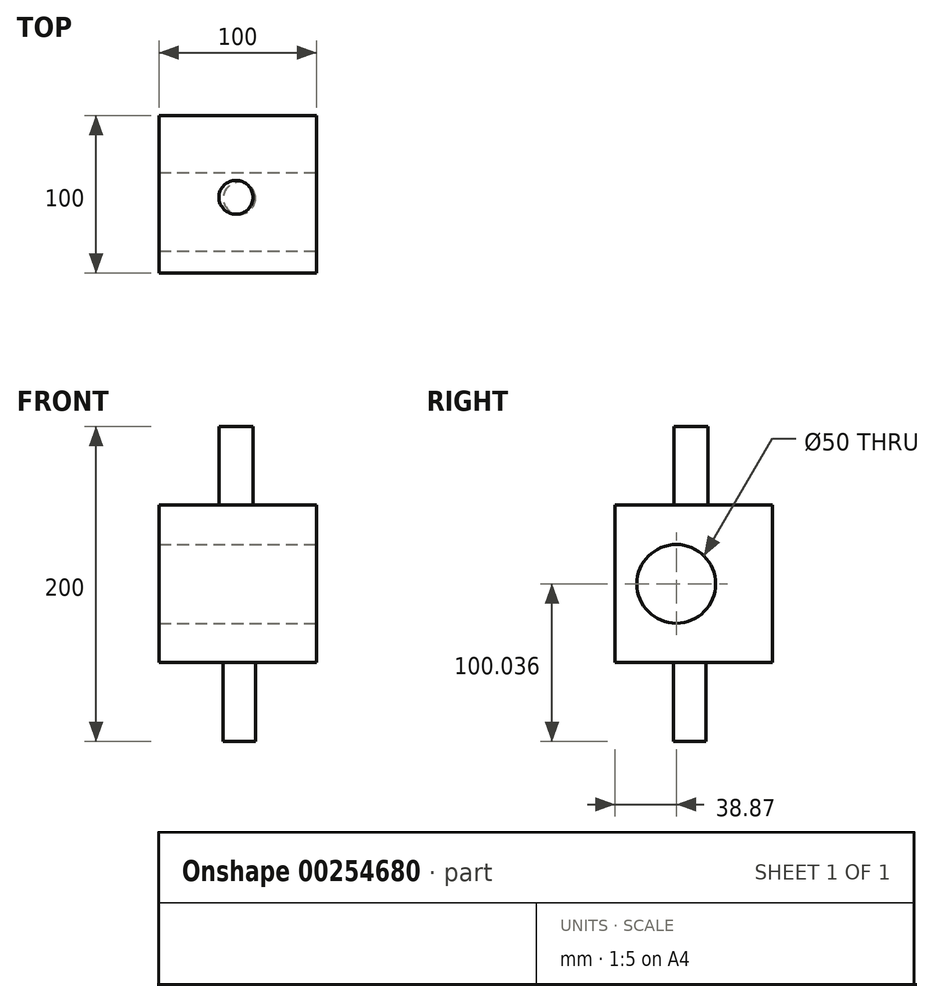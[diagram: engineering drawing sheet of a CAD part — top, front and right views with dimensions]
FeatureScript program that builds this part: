
annotation { "Feature Type Name" : "Feature", "Feature Type Description" : "" }
export const myFeature = defineFeature(function(context is Context, id is Id, definition is map)
    precondition{}
    {
        {
            var Q0;
            Q0=qCreatedBy(makeId("Front.planeOp"),FACE);
            var sketch = newSketch(context, id + "F0", { "sketchPlane" : qUnion([Q0])});
            skLineSegment(sketch, "E0.bottom", {"start": v(0, 0) * mm, "end": v(100, 0) * mm});
            skLineSegment(sketch, "E0.top", {"start": v(0, 100) * mm, "end": v(100, 100) * mm});
            skLineSegment(sketch, "E0.left", {"start": v(0, 0) * mm, "end": v(0, 100) * mm});
            skLineSegment(sketch, "E0.right", {"start": v(100, 0) * mm, "end": v(100, 100) * mm});
            skSolve(sketch);
        }
        {
            var Q0;
            Q0 = qSketchRegion(id + "F0", true);
            extrude(context, id + "F1", {"entities" : qUnion([Q0]), "depth" : 100 * mm});
        }
        {
            var Q0;
            Q0=makeQuery(id+"F1.opExtrude","SWEPT_FACE",FACE,{"disambiguationData":[OSD([sQuery(id+"F0.wireOp",EDGE,"E0.top")])]});
            var sketch = newSketch(context, id + "F2", { "sketchPlane" : qUnion([Q0])});
            skCircle(sketch, "E1", {"center": v(48.79, -51.93) * mm, "radius": 10.8 * mm});
            skSolve(sketch);
        }
        {
            var Q0;
            Q0 = qSketchRegion(id + "F2", true);
            extrude(context, id + "F3", {"entities" : qUnion([Q0]), "operationType" : NewBodyOperationType.ADD, "depth" : 50 * mm});
        }
        {
            var Q0;
            Q0=makeQuery(id+"F3.opExtrude","CAP_FACE",FACE,{"disambiguationData":[OSD([sQuery(id+"F2.wireOp",EDGE,"E1")])],"isStart":false});
            var sketch = newSketch(context, id + "F4", { "sketchPlane" : qUnion([Q0])});
            skSolve(sketch);
        }
        {
            var Q0;
            Q0=makeQuery(id+"F1.opExtrude","SWEPT_FACE",FACE,{"disambiguationData":[OSD([sQuery(id+"F0.wireOp",EDGE,"E0.bottom")])]});
            var sketch = newSketch(context, id + "F5", { "sketchPlane" : qUnion([Q0])});
            skCircle(sketch, "E2", {"center": v(50.98, 52.56) * mm, "radius": 10.23 * mm});
            skSolve(sketch);
        }
        {
            var Q0;
            Q0 = qSketchRegion(id + "F5", true);
            extrude(context, id + "F6", {"entities" : qUnion([Q0]), "operationType" : NewBodyOperationType.ADD, "depth" : 50 * mm});
        }
        {
            var Q0;
            Q0=makeQuery(id+"F1.opExtrude","SWEPT_FACE",FACE,{"disambiguationData":[OSD([sQuery(id+"F0.wireOp",EDGE,"E0.right")])]});
            var sketch = newSketch(context, id + "F7", { "sketchPlane" : qUnion([Q0])});
            skCircle(sketch, "E3", {"center": v(-61.13, 50.04) * mm, "radius": 10.4 * mm});
            skSolve(sketch);
        }
        {
            var Q0;
            Q0=sQuery(id+"F7.wireOp",VERTEX,"E3.center");
            var Q1;
            Q1=makeQuery(id+"F1.opExtrude","SWEPT_BODY",BODY,{"disambiguationData":[OSD([sQuery(id+"F0.wireOp",EDGE,"E0.bottom"),sQuery(id+"F0.wireOp",EDGE,"E0.top"),sQuery(id+"F0.wireOp",EDGE,"E0.left"),sQuery(id+"F0.wireOp",EDGE,"E0.right")])]});
            hole(context, id + "F8", {"style" : HoleStyle.SIMPLE, "endStyle" : HoleEndStyle.THROUGH, "holeDiameter" : 50 * mm, "tappedDepth" : 12.7 * mm, "tapClearance" : 3, "locations" : qUnion([Q0]), "scope" : qUnion([Q1])});
        }
    });
